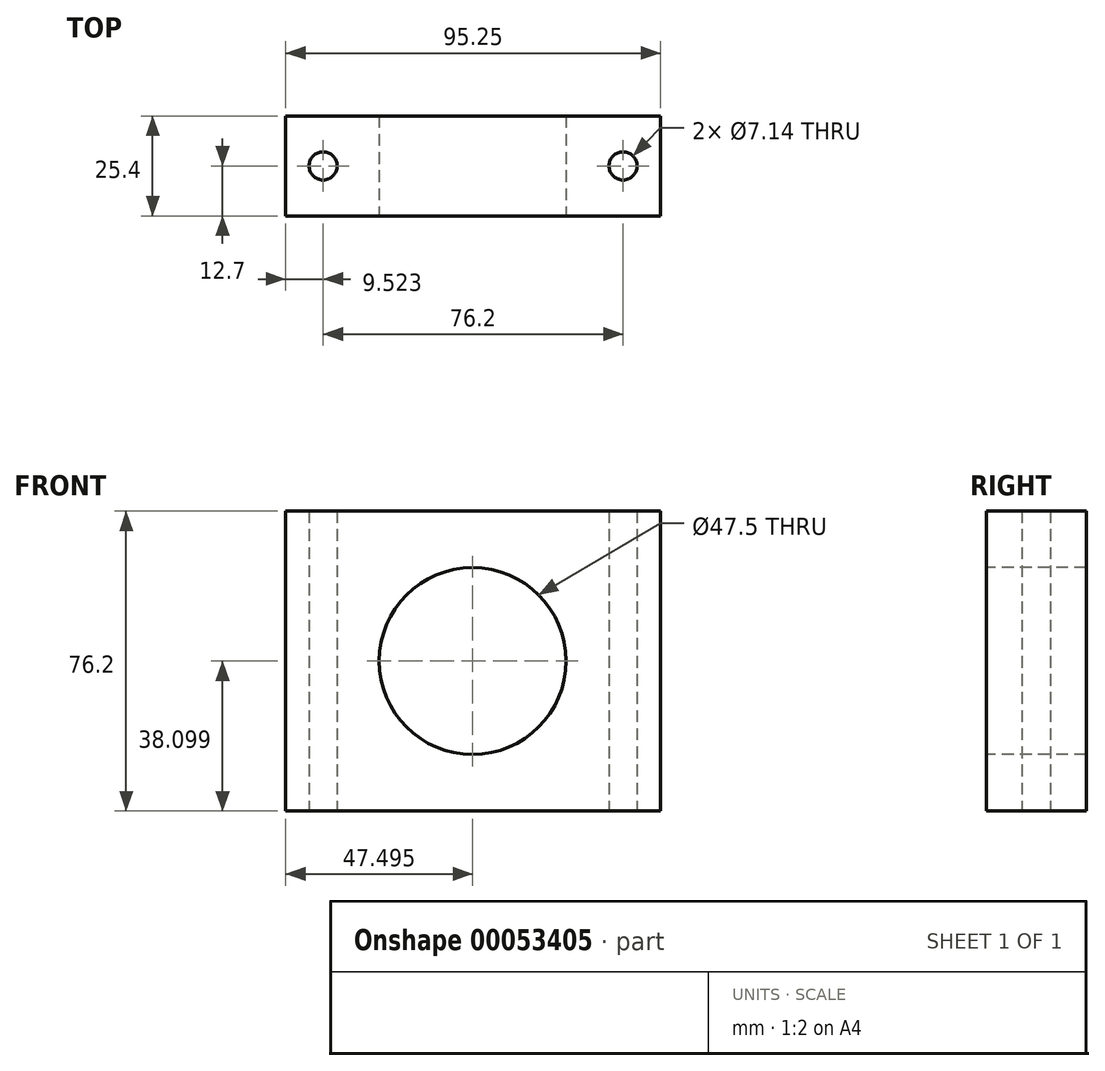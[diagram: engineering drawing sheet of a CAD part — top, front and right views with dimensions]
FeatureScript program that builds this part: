
annotation { "Feature Type Name" : "Feature", "Feature Type Description" : "" }
export const myFeature = defineFeature(function(context is Context, id is Id, definition is map)
    precondition{}
    {
        {
            var Q0;
            Q0=qCreatedBy(makeId("Front.planeOp"),FACE);
            var sketch = newSketch(context, id + "F0", { "sketchPlane" : qUnion([Q0])});
            skLineSegment(sketch, "E0.bottom", {"start": v(-47.3, 38.5) * mm, "end": v(47.96, 38.5) * mm});
            skLineSegment(sketch, "E0.top", {"start": v(-47.3, -37.7) * mm, "end": v(47.96, -37.7) * mm});
            skLineSegment(sketch, "E0.left", {"start": v(-47.3, 38.5) * mm, "end": v(-47.3, -37.7) * mm});
            skLineSegment(sketch, "E0.right", {"start": v(47.96, 38.5) * mm, "end": v(47.96, -37.7) * mm});
            skSolve(sketch);
        }
        {
            var Q0;
            Q0=makeQuery(id+"F0.imprint","IMPRINT",FACE,{"disambiguationData":[TD([[makeQuery(id+"F0.imprint","IMPRINT",EDGE,{"derivedFrom":sQuery(id+"F0.wireOp",EDGE,"E0.bottom")}),-1.0]])]});
            extrude(context, id + "F1", {"entities" : qUnion([Q0]), "depth" : 25.4 * mm});
        }
        {
            var Q0;
            Q0=makeQuery(id+"F1.opExtrude","CAP_FACE",FACE,{"disambiguationData":[OSD([sQuery(id+"F0.wireOp",EDGE,"E0.bottom"),sQuery(id+"F0.wireOp",EDGE,"E0.top"),sQuery(id+"F0.wireOp",EDGE,"E0.left"),sQuery(id+"F0.wireOp",EDGE,"E0.right")])],"isStart":false});
            var sketch = newSketch(context, id + "F2", { "sketchPlane" : qUnion([Q0])});
            skCircle(sketch, "E1", {"center": v(0.2, 0.4) * mm, "radius": 23.75 * mm});
            skSolve(sketch);
        }
        {
            var Q0;
            Q0 = qSketchRegion(id + "F2", true);
            extrude(context, id + "F3", {"entities" : qUnion([Q0]), "operationType" : NewBodyOperationType.REMOVE, "endBound" : BoundingType.THROUGH_ALL, "oppositeDirection" : true, "depth" : 25.4 * mm});
        }
        {
            var Q0;
            Q0=makeQuery(id+"F1.opExtrude","SWEPT_FACE",FACE,{"disambiguationData":[OSD([sQuery(id+"F0.wireOp",EDGE,"E0.top")])]});
            var sketch = newSketch(context, id + "F4", { "sketchPlane" : qUnion([Q0])});
            skCircle(sketch, "E2", {"center": v(-37.77, 12.7) * mm, "radius": 3.57 * mm});
            skSolve(sketch);
        }
        {
            var Q0;
            Q0 = qSketchRegion(id + "F4", true);
            extrude(context, id + "F5", {"entities" : qUnion([Q0]), "operationType" : NewBodyOperationType.REMOVE, "endBound" : BoundingType.THROUGH_ALL, "oppositeDirection" : true, "depth" : 25.4 * mm});
        }
        {
            var Q0;
            Q0=makeQuery(id+"F1.opExtrude","SWEPT_FACE",FACE,{"disambiguationData":[OSD([sQuery(id+"F0.wireOp",EDGE,"E0.top")])]});
            var sketch = newSketch(context, id + "F6", { "sketchPlane" : qUnion([Q0])});
            skCircle(sketch, "E3", {"center": v(38.43, 12.7) * mm, "radius": 3.57 * mm});
            skSolve(sketch);
        }
        {
            var Q0;
            Q0 = qSketchRegion(id + "F6", true);
            extrude(context, id + "F7", {"entities" : qUnion([Q0]), "operationType" : NewBodyOperationType.REMOVE, "endBound" : BoundingType.THROUGH_ALL, "oppositeDirection" : true, "depth" : 25.4 * mm});
        }
    });
